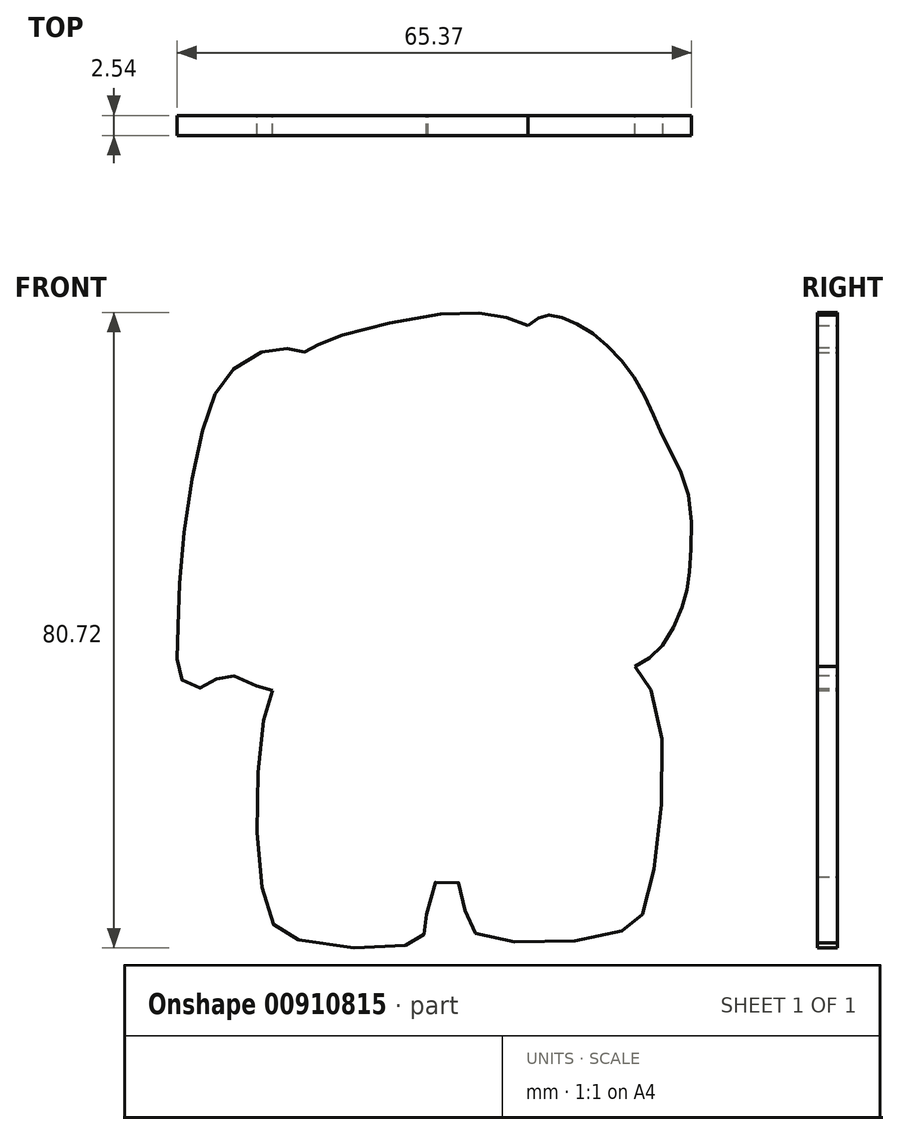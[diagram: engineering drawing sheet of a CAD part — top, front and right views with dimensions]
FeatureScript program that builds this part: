
annotation { "Feature Type Name" : "Feature", "Feature Type Description" : "" }
export const myFeature = defineFeature(function(context is Context, id is Id, definition is map)
    precondition{}
    {
        {
            var Q0;
            Q0=qCreatedBy(makeId("Front.planeOp"),FACE);
            var sketch = newSketch(context, id + "F0", { "sketchPlane" : qUnion([Q0])});
            skFitSpline(sketch, "E0", {"points": [v(69.14, 109.84) * mm, v(65.64, 111.03) * mm, v(57.53, 111.2) * mm, v(43.45, 107.87) * mm, v(42, 107.02) * mm, v(40.12, 106.42) * mm, v(37.73, 107.02) * mm, v(31.92, 104.46) * mm, v(28.34, 98.31) * mm, v(25.18, 81.16) * mm, v(24.58, 68.86) * mm, v(25.01, 65.02) * mm, v(27.31, 63.74) * mm, v(29.45, 64.85) * mm, v(31.5, 65.36) * mm, v(35, 63.91) * mm, v(36.7, 63.49) * mm], "startDerivative": vector(-60.3, 24.55) * mm, "endDerivative": vector(40.88, -5.89) * mm});
            skFitSpline(sketch, "E1", {"points": [v(36.7, 63.49) * mm, v(35.75, 60.64) * mm, v(34.8, 51.53) * mm, v(35.13, 39.78) * mm, v(36.7, 33.93) * mm, v(38.15, 32.42) * mm, v(47.02, 30.8) * mm, v(54.57, 31.33) * mm, v(55.53, 32) * mm, v(56.44, 33.39) * mm, v(56.26, 34.6) * mm, v(56.92, 38.4) * mm, v(58.8, 39.78) * mm, v(60.79, 38.4) * mm, v(61.15, 35.5) * mm, v(61.87, 33.2) * mm, v(64.47, 31.88) * mm, v(75.57, 31.7) * mm, v(82.03, 33.33) * mm, v(83.54, 34.77) * mm, v(85.41, 42.62) * mm, v(86.14, 57.53) * mm, v(84.2, 64.71) * mm, v(82.76, 66.52) * mm], "startDerivative": vector(-29.13, -69.73) * mm, "endDerivative": vector(-47.9, 48.2) * mm});
            skFitSpline(sketch, "E2", {"points": [v(82.76, 66.52) * mm, v(86.04, 68.98) * mm, v(88.86, 74.55) * mm, v(89.72, 79.21) * mm, v(89.37, 88.82) * mm, v(86.56, 95.1) * mm, v(83.92, 100.93) * mm, v(80.46, 106) * mm, v(76.44, 109.4) * mm, v(72.9, 111) * mm, v(70.95, 111.03) * mm, v(69.14, 109.84) * mm], "startDerivative": vector(41.58, 23.18) * mm, "endDerivative": vector(-29.56, -24.57) * mm});
            skSolve(sketch);
        }
        {
            var Q0;
            Q0 = qSketchRegion(id + "F0", true);
            extrude(context, id + "F1", {"entities" : qUnion([Q0]), "depth" : 2.54 * mm, "offsetDistance" : 25.4 * mm});
        }
    });
